# Revit family: Sink_Valve-Two_Handle-Grohe-Non_Rapido-33885000
name_source: partatom
category: Plumbing Fixtures
revit_build: Autodesk Revit 2018 (Build: 20170223_1515(x64)
units: mm (PartAtom-declared; Revit-internal decimal feet)

## family parameters
Cut with Voids When Loaded = No
Host = Face
OmniClass Number = 23.45.05.14.14
OmniClass Title = Sinks/Lavatories
Part Type = Normal
Room Calculation Point = No
Round Connector Dimension = Use Diameter
Shared = Yes

## types (1)
- 33885000
    Assembly Code = D2020300
    CW Connection = Yes
    CWFU = 1.5
    Cold Water Connection Diameter = 1/2"
    Default Elevation = 0"
    Description = Non Rapido 3-Hole Wall Mount Faucet Rough-In Valve: GROHE SilkMove for a lifetime of smooth operation, 1/2 in. NPT Female inlets, 8 in. On-Center rough-in valve, GROHE SilkMove ceramic cartridge.
    Finish = Metal-Grohe-Cast Brass
    HW Connection = Yes
    HWFU = 1.5
    Hot Water Connection Diameter = 1/2"
    IAPMO Compliance = Energy Policy Act of 1992, NSF 61, ASME A112.18.1/CSA B125.1 and US Federal and State material regulations.
    Installation Type = Wall Mount
    Manufacturer = Grohe
    Material = Metal-Grohe-Cast Brass
    Model = 33885000
    Price = Prices may vary. Please consult Manufacturer Representative for most up-to-date price list.
    Product Documentation Link = https://americanstandard.box.com
    Product Page URL = https://www.grohe.us
    Revised Date = 07/21/2021
    Tempered Water Connection = Yes
    Tempered Water Connection Diameter = 1/2"
    URL = https://www.grohe.us
    WFU = 2
    Width = 11 1/8"

## geometry (parser evidence)
native form markers: Sweep x2
no freeform markers — native parametric forms only
